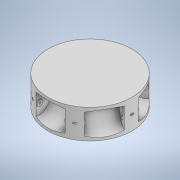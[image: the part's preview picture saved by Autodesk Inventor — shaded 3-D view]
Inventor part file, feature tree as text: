
AUTODESK INVENTOR PART (.ipt)
format: ipt  version: 2021 (Build 250183000, 183)  size: 370,688 bytes
history: native  units: in
note: dims shown in document units (in); Inventor stores cm internally (conversion verified against a paired STEP export)
features: revolve x6, sketch x1, extrude x1, mirror x1
ambient origin geometry x8: Origin, YZ Plane, XZ Plane, XY Plane, X Axis, Y Axis, Z Axis, Center Point
bodies: Solid1 (feature_tree)
feature tree (9):
  sketch  "Sketch1"  dims[d0=1.9685in d1=0.0787in d2=2.3622in d4=360.0deg d6=0.5906in d7=0.6299in d8=0.0787in d14=0.315in d15=0.0in d25=0.0394in d31=90.0deg d32=2.3622in d34=360.0deg d36=90.0deg d37=90.0deg d38=90.0deg d39=90.0deg d40=90.0deg]
  extrude  "Extrusion1"  Depth=0.315in
  revolve  "Revolution8"  Angle=360.0deg
  revolve  "Revolution9"  [1 undecoded]
  revolve  "Revolution10"  [1 undecoded]
  revolve  "Revolution11"  [1 undecoded]
  revolve  "Revolution12"  [1 undecoded]
  revolve  "Revolution13"  [1 undecoded]
  mirror  "Mirror1"
note: 5 required parameter values undecoded (feature->parameter linkage not recoverable at this tier; creation-order binding heuristic only, values carry confidence <= 0.55)
